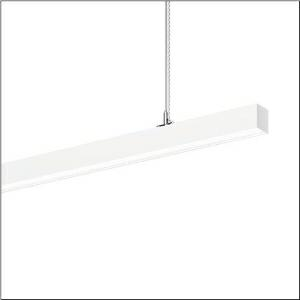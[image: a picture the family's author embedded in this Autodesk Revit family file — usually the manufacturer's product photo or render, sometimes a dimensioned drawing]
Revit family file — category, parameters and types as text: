
# Revit family: silica_r__21_51mx30tat4w_7b2a
name_source: partatom
category: Lighting Fixtures
units: mm (PartAtom-declared; Revit-internal decimal feet)

## family parameters
Cut with Voids When Loaded = No
Host = Face
Light Source = No
Part Type = Normal
Room Calculation Point = No
Round Connector Dimension = Use Diameter
Shared = No

## types (1)
- --- (1 x LED, 4120 lm, 33.8 W, 6500K)
    Apparent Load = 34 VA
    CIE Flux Codes = 47 79 96 58 100
    Color Rendering = 80
    Color Temperature = 6500K
    Default Elevation = 1800 mm
    Description = Silica® 21, office luminaire, primary optical cover: cover, of PMMA, opal, light emission: direct/indirect distribution, primary light characteristic: symmetric, installation type: suspended mounting, LED, rated luminous flux: 4.120lm, luminous efficacy: 116lm/W, light colour: 8tw, colour temperature: 2700..6500K, control gear: ECG DALI, with terminal, 3+2-pole, max. 2.5mm², mains connection: 220..240V, AC, 50/60Hz, rated input power: 35.5W, luminaire housing, of aluminium, traffic white (RAL 9016), length: 1.204mm, width: 53mm, height: 53mm, protection rating (complete): IP20, insulation class (complete): insulation class I (protective earthing), certification: CE, permissible operating ambient temperature: 0..+35°C, standard: EN 50419, packaging unit: 1 piece
    Height = 53 mm
    Lamp = 1 x LED
    Lamp Light Flux = 4120 lm
    Lamp Power = 33.8 W
    Lamp count = 1
    Length = 1204 mm
    Luminous efficacy = 122 lm/W
    Manufacturer = Siteco
    ModVariant = No
    Model = 51MX30TAT4W
    Mounting Place = Ceiling
    Mounting Type = Pendant
    Number of Poles = 1
    OnlyDefault = Yes
    Power Factor = 1
    Product Name = Silica® 21
    Product group = office luminaire | ceiling pendant
    ProductGroupID = 905
    Protection Class = Protection class I
    Protection Degree = IP 20
    RLX_Detail_Level = 1
    RlxData = <blob elided: 18145 chars, md5=3d621d42>
    Socket = socket
    Standby Power = 0 W
    System Light Flux = 4120 lm
    System Power = 34 W
    Type Comments = individual setting
    Type Image = l_1251642.jpg
    URL = http://relux.com
    VarID = @adj_045747
    Voltage = 0 V
    Weight = 0.00 kg
    Width = 53 mm

## geometry (parser evidence)
native form markers: Blend x4, Sweep x12
no freeform markers — native parametric forms only
